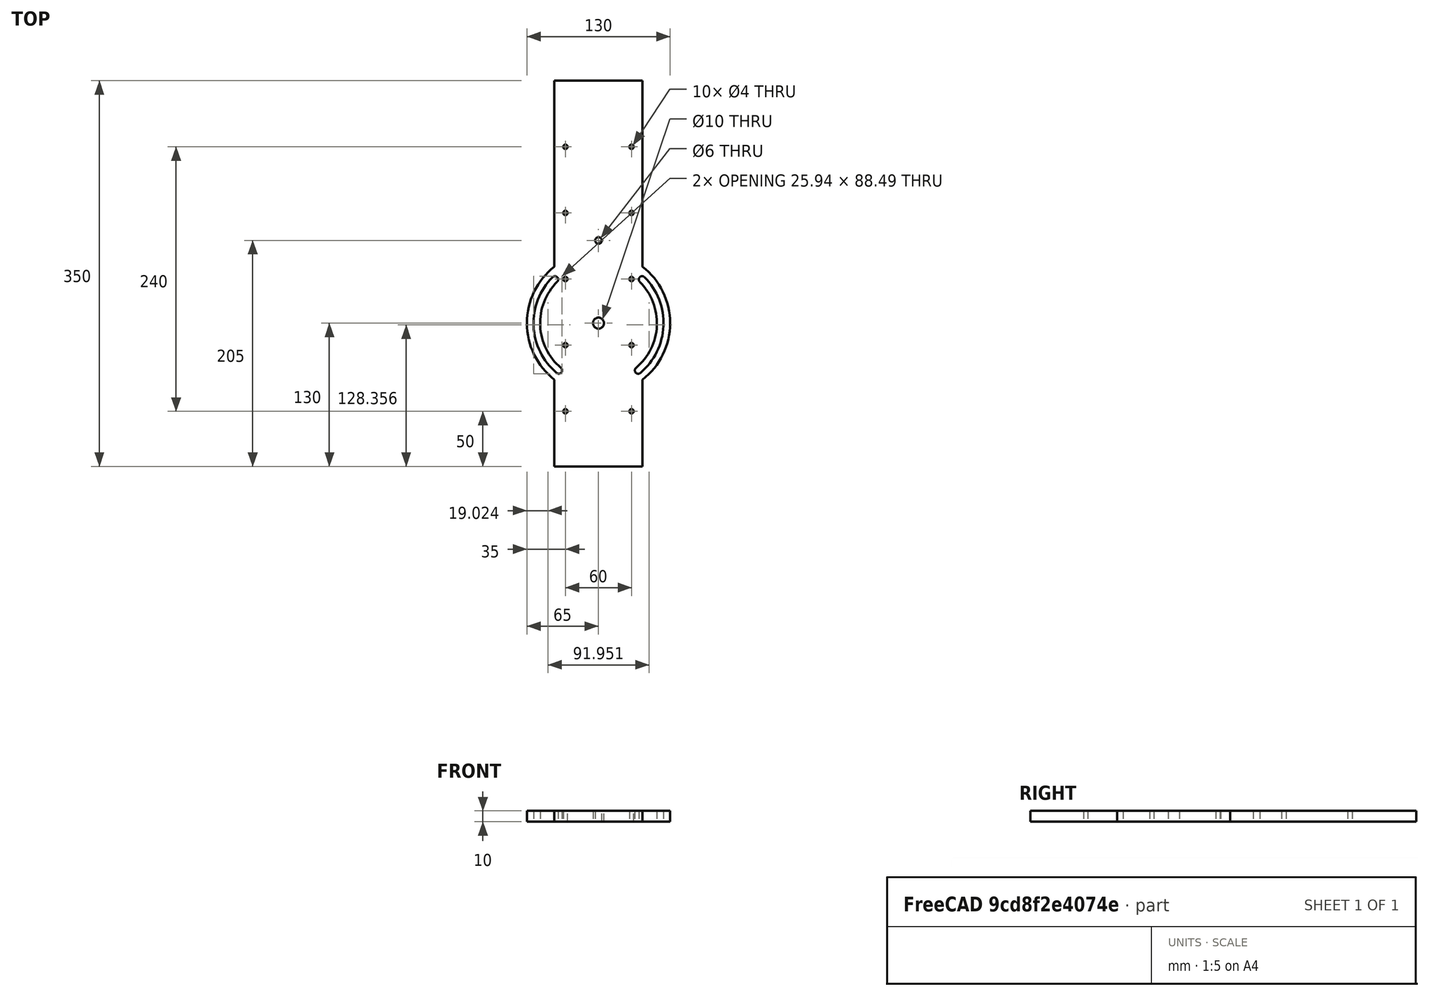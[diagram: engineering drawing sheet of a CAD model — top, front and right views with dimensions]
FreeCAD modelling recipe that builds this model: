
FCSTD DOCUMENT  (FreeCAD 0.21R33771 (Git))
Label: PiastraMandrinoRotante
License: All rights reserved
LicenseURL: http://en.wikipedia.org/wiki/All_rights_reserved
objects: Sketcher::SketchObject×1, PartDesign::Pad×1, PartDesign::CoordinateSystem×1, PartDesign::Body×1
note: 5 computed .brp shape members not serialized (recipe doc carries the construction recipe); baked Part::Feature solids carry a one-line shape summary decoded from their .brp

FEATURE [Sketcher::SketchObject] Sketch
  FullyConstrained = false
  MapMode = 5
  Support = -> [XY_Plane]
  sketch-geometry (41):
    g0: LineSegment StartX=-2.13e-14 StartY=0 StartZ=0 EndX=80 EndY=0 EndZ=0
    g1: LineSegment StartX=80 StartY=0 StartZ=0 EndX=80 EndY=78.7652 EndZ=0
    g2: LineSegment StartX=80 StartY=350 StartZ=0 EndX=0 EndY=350 EndZ=0
    g3: LineSegment StartX=-7.1e-15 StartY=350 StartZ=0 EndX=-7.1e-15 EndY=181.235 EndZ=0
    g4: Circle CenterX=10 CenterY=50 CenterZ=0 NormalX=0 NormalY=0 NormalZ=1 AngleXU=0 Radius=2
    g5: Circle CenterX=10 CenterY=110 CenterZ=0 NormalX=0 NormalY=0 NormalZ=1 AngleXU=0 Radius=2
    g6: LineSegment StartX=10 StartY=50 StartZ=0 EndX=10 EndY=110 EndZ=0
    g7: Circle CenterX=10 CenterY=170 CenterZ=0 NormalX=0 NormalY=0 NormalZ=1 AngleXU=0 Radius=2
    g8: LineSegment StartX=10 StartY=110 StartZ=0 EndX=10 EndY=170 EndZ=0
    g9: Circle CenterX=10 CenterY=230 CenterZ=0 NormalX=0 NormalY=0 NormalZ=1 AngleXU=0 Radius=2
    g10: LineSegment StartX=10 StartY=170 StartZ=0 EndX=10 EndY=230 EndZ=0
    g11: Circle CenterX=10 CenterY=290 CenterZ=0 NormalX=0 NormalY=0 NormalZ=1 AngleXU=0 Radius=2
    g12: LineSegment StartX=10 StartY=230 StartZ=0 EndX=10 EndY=290 EndZ=0
    g13: Circle CenterX=70 CenterY=50 CenterZ=0 NormalX=0 NormalY=0 NormalZ=1 AngleXU=0 Radius=2
    g14: LineSegment StartX=10 StartY=50 StartZ=0 EndX=70 EndY=50 EndZ=0
    g15: Circle CenterX=70 CenterY=110 CenterZ=0 NormalX=0 NormalY=0 NormalZ=1 AngleXU=0 Radius=2
    g16: LineSegment StartX=70 StartY=50 StartZ=0 EndX=70 EndY=110 EndZ=0
    g17: Circle CenterX=70 CenterY=170 CenterZ=0 NormalX=0 NormalY=0 NormalZ=1 AngleXU=0 Radius=2
    g18: LineSegment StartX=70 StartY=110 StartZ=0 EndX=70 EndY=170 EndZ=0
    g19: Circle CenterX=70 CenterY=230 CenterZ=0 NormalX=0 NormalY=0 NormalZ=1 AngleXU=0 Radius=2
    g20: LineSegment StartX=70 StartY=170 StartZ=0 EndX=70 EndY=230 EndZ=0
    g21: Circle CenterX=70 CenterY=290 CenterZ=0 NormalX=0 NormalY=0 NormalZ=1 AngleXU=0 Radius=2
    g22: LineSegment StartX=70 StartY=230 StartZ=0 EndX=70 EndY=290 EndZ=0
    g23: Circle CenterX=40 CenterY=130 CenterZ=0 NormalX=0 NormalY=0 NormalZ=1 AngleXU=0 Radius=5
    g24: LineSegment StartX=80 StartY=181.235 StartZ=0 EndX=80 EndY=350 EndZ=0
    g25: LineSegment StartX=-2.13e-14 StartY=78.7652 StartZ=0 EndX=-2.13e-14 EndY=0 EndZ=0
    g26: ArcOfCircle CenterX=40 CenterY=130 CenterZ=0 NormalX=0 NormalY=0 NormalZ=1 AngleXU=0 Radius=65 StartAngle=5.37526 EndAngle=7.19111
    g27: ArcOfCircle CenterX=40 CenterY=130 CenterZ=0 NormalX=0 NormalY=0 NormalZ=1 AngleXU=0 Radius=65 StartAngle=2.23367 EndAngle=4.04952
    g28: Circle CenterX=40 CenterY=130 CenterZ=0 NormalX=0 NormalY=0 NormalZ=1 AngleXU=0 Radius=56
    g29: LineSegment StartX=40 StartY=130 StartZ=0 EndX=40 EndY=205 EndZ=0
    g30: Circle CenterX=40 CenterY=205 CenterZ=0 NormalX=0 NormalY=0 NormalZ=1 AngleXU=0 Radius=3
    g31: ArcOfCircle CenterX=40 CenterY=130 CenterZ=0 NormalX=0 NormalY=0 NormalZ=1 AngleXU=0 Radius=59 StartAngle=2.35619 EndAngle=4.01426
    g32: ArcOfCircle CenterX=40 CenterY=130 CenterZ=0 NormalX=0 NormalY=0 NormalZ=1 AngleXU=0 Radius=53 StartAngle=2.35619 EndAngle=4.01426
    g33: LineSegment StartX=40 StartY=130 StartZ=0 EndX=-66.264 EndY=236.264 EndZ=0
    g34: LineSegment StartX=40 StartY=130 StartZ=0 EndX=-32.4746 EndY=43.6281 EndZ=0
    g35: ArcOfCircle CenterX=0.40202 CenterY=169.598 CenterZ=0 NormalX=0 NormalY=0 NormalZ=1 AngleXU=0 Radius=3 StartAngle=5.49778 EndAngle=8.63938
    g36: ArcOfCircle CenterX=4.00389 CenterY=87.1015 CenterZ=0 NormalX=0 NormalY=0 NormalZ=1 AngleXU=0 Radius=3 StartAngle=4.01426 EndAngle=7.15585
    g37: ArcOfCircle CenterX=40 CenterY=130 CenterZ=0 NormalX=0 NormalY=0 NormalZ=1 AngleXU=0 Radius=53 StartAngle=5.41052 EndAngle=7.06858
    g38: ArcOfCircle CenterX=79.598 CenterY=169.598 CenterZ=0 NormalX=0 NormalY=0 NormalZ=1 AngleXU=0 Radius=3 StartAngle=0.785398 EndAngle=3.927
    g39: ArcOfCircle CenterX=40 CenterY=130 CenterZ=0 NormalX=0 NormalY=0 NormalZ=1 AngleXU=0 Radius=59 StartAngle=5.41052 EndAngle=7.06858
    g40: ArcOfCircle CenterX=75.9961 CenterY=87.1015 CenterZ=0 NormalX=0 NormalY=0 NormalZ=1 AngleXU=0 Radius=3 StartAngle=2.26893 EndAngle=5.41052
  constraints (108):
    c: Coincident(g0,g1)
    c: Coincident(g24,g2)
    c: Coincident(g2,g3)
    c: Coincident(g25,g0)
    c: Horizontal(g0)
    c: Horizontal(g2)
    c: Vertical(g1)
    c: Vertical(g3)
    c: Coincident(g0,g-1)
    c: DistanceX(g0,g0) = 80
    c: DistanceY(g25,g3) = 350
    c: DistanceX(g0,g4) = 10
    c: DistanceY(g0,g4) = 50
    c: Radius(g4) = 2
    c: Radius(g5) = 2
    c: Coincident(g4,g6)
    c: Coincident(g5,g6)
    c: Distance(g6) = 60
    c: Angle(g6) = 1.5708
    c: Radius(g7) = 2
    c: Coincident(g5,g8)
    c: Coincident(g7,g8)
    c: Equal(g6,g8)
    c: Parallel(g8,g6)
    c: Radius(g9) = 2
    c: Coincident(g7,g10)
    c: Coincident(g9,g10)
    c: Equal(g6,g10)
    c: Parallel(g10,g6)
    c: Radius(g11) = 2
    c: Coincident(g9,g12)
    c: Coincident(g11,g12)
    c: Equal(g6,g12)
    c: Parallel(g12,g6)
    c: Radius(g13) = 2
    c: Coincident(g4,g14)
    c: Coincident(g13,g14)
    c: Distance(g14) = 60
    c: Perpendicular(g14,g6)
    c: Radius(g15) = 2
    c: Coincident(g13,g16)
    c: Coincident(g15,g16)
    c: Equal(g6,g16)
    c: Parallel(g16,g6)
    c: Radius(g17) = 2
    c: Coincident(g15,g18)
    c: Coincident(g17,g18)
    c: Equal(g6,g18)
    c: Parallel(g18,g6)
    c: Radius(g19) = 2
    c: Coincident(g17,g20)
    c: Coincident(g19,g20)
    c: Equal(g6,g20)
    c: Parallel(g20,g6)
    c: Radius(g21) = 2
    c: Coincident(g19,g22)
    c: Coincident(g21,g22)
    c: Equal(g6,g22)
    c: Parallel(g22,g6)
    c: Radius(g23) = 5
    c: Coincident(g27,g25)
    c: Coincident(g27,g3)
    c: Vertical(g25)
    c: Equal(g27,g26)
    c: Vertical(g24)
    c: Equal(g0,g2)
    c: Radius(g27) = 65
    c: Coincident(g24,g26)
    c: Coincident(g26,g1)
    c: Equal(g25,g1)
    c: Coincident(g27,g23)
    c: Equal(g3,g24)
    c: Coincident(g28,g23)
    c: Radius(g28) = 56
    c: Coincident(g29,g23)
    c: Vertical(g29)
    c: Coincident(g30,g29)
    c: Radius(g30) = 3
    c: DistanceY(g29,g29) = 75
    c: PointOnObject(g3,g-2)
    c: Coincident(g31,g23)
    c: Coincident(g32,g23)
    c: Coincident(g33,g23)
    c: Coincident(g34,g23)
    c: Angle(g33,g34) = 1.65806
    c: Angle(g29,g33) = 0.785398
    c: Radius(g31) = 59
    c: Radius(g32) = 53
    c: PointOnObject(g35,g33)
    c: Radius(g35) = 3
    c: PointOnObject(g36,g34)
    c: Equal(g36,g35)
    c: PointOnObject(g31,g33)
    c: PointOnObject(g35,g33)
    c: Coincident(g35,g32)
    c: PointOnObject(g31,g34)
    c: PointOnObject(g36,g34)
    c: Coincident(g36,g32)
    c: PointOnObject(g36,g28)
    c: PointOnObject(g35,g28)
    c: DistanceY(g0,g23) = 130
    c: DistanceX(g0,g26) = 40
    c: Radius(g39) = 59
    c: Radius(g37) = 53
    c: Radius(g38) = 3
    c: Equal(g40,g38)
    c: Coincident(g38,g37)
    c: Coincident(g40,g37)
FEATURE [PartDesign::Pad] Pad
  Direction = (0,0,1)
  Length = 10
  Length2 = 10
  Profile = -> Sketch
  ReferenceAxis = -> Sketch [N_Axis]
  Type = 0
FEATURE [PartDesign::CoordinateSystem] LCS_PiastraRotazioneUtensile
  AttacherType = Attacher::AttachEngine3D
  MapMode = 11
  Placement = pos=(40,130,10) rot=(0,0,1;1.5708rad)
  Support = -> [Pad]
FEATURE [PartDesign::Body] Body
  Group = -> [Sketch,Pad,LCS_PiastraRotazioneUtensile]
  Origin = -> Origin
  Tip = -> Pad
